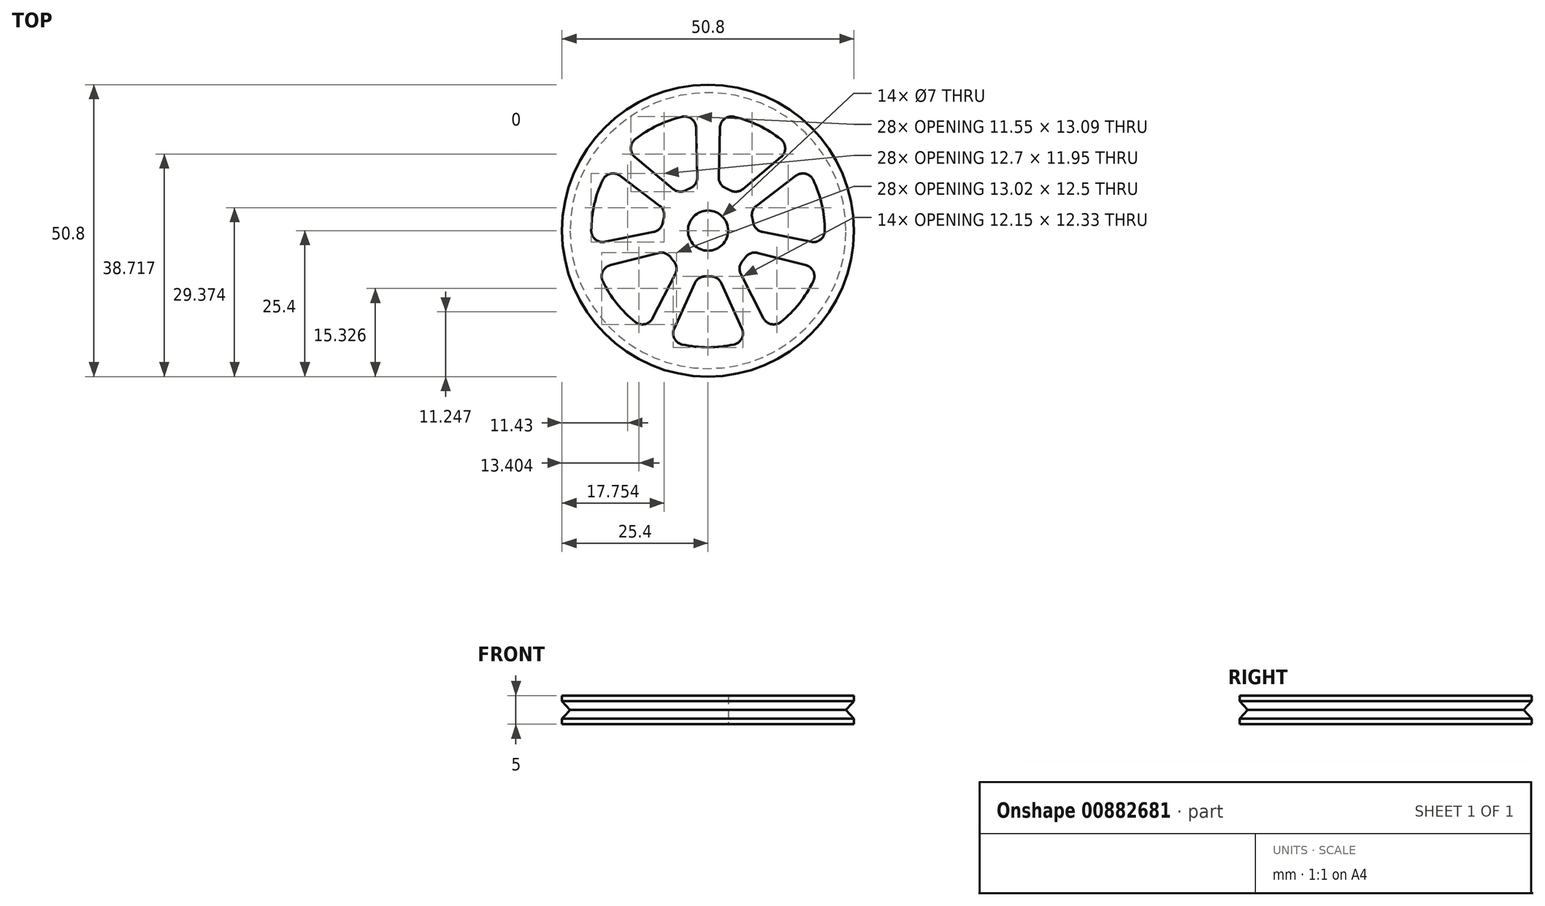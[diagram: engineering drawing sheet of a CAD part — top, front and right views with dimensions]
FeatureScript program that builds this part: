
annotation { "Feature Type Name" : "Feature", "Feature Type Description" : "" }
export const myFeature = defineFeature(function(context is Context, id is Id, definition is map)
    precondition{}
    {
        {
            var Q0;
            Q0=qCreatedBy(makeId("Top.planeOp"),FACE);
            var sketch = newSketch(context, id + "F0", { "sketchPlane" : qUnion([Q0])});
            skCircle(sketch, "E0", {"center": v(0, 0) * mm, "radius": 25.4 * mm});
            skCircle(sketch, "E1", {"center": v(0, 0) * mm, "radius": 3.5 * mm});
            skArc(sketch, "E2.0", {"start": v(-3.1, 7.37) * mm, "mid": v(-3.47, 7.2) * mm, "end": v(-3.83, 7.02) * mm});
            skArc(sketch, "E3.0", {"start": v(-4.52, 19.81) * mm, "mid": v(-8.82, 18.3) * mm, "end": v(-12.67, 15.89) * mm});
            skLineSegment(sketch, "E4.0", {"start": v(-1.87, 9.27) * mm, "end": v(-2.08, 17.9) * mm});
            skLineSegment(sketch, "E5.0", {"start": v(1.87, 9.27) * mm, "end": v(2.08, 17.9) * mm});
            skPoint(sketch, "E6.start.orphan", {"position": v(0, 12.84) * mm});
            skPoint(sketch, "E7.visualSharp", {"position": v(-2.13, 20.2) * mm});
            skArc(sketch, "E7.filletArc", {"start": v(-2.08, 17.9) * mm, "mid": v(-2.85, 19.44) * mm, "end": v(-4.52, 19.81) * mm});
            skPoint(sketch, "E8.visualSharp", {"position": v(-1.83, 7.78) * mm});
            skArc(sketch, "E8.filletArc", {"start": v(-3.1, 7.37) * mm, "mid": v(-2.2, 8.13) * mm, "end": v(-1.87, 9.27) * mm});
            skPoint(sketch, "E9.visualSharp", {"position": v(2.13, 20.2) * mm});
            skArc(sketch, "E9.filletArc", {"start": v(4.52, 19.81) * mm, "mid": v(2.85, 19.44) * mm, "end": v(2.08, 17.9) * mm});
            skPoint(sketch, "E10.visualSharp", {"position": v(1.83, 7.78) * mm});
            skArc(sketch, "E10.filletArc", {"start": v(1.87, 9.27) * mm, "mid": v(2.2, 8.13) * mm, "end": v(3.1, 7.37) * mm});
            skArc(sketch, "E11.1.0", {"start": v(-15.3, 9.54) * mm, "mid": v(-16.97, 9.9) * mm, "end": v(-18.3, 8.82) * mm});
            skLineSegment(sketch, "E11.1.1", {"start": v(-8.4, 4.32) * mm, "end": v(-15.3, 9.54) * mm});
            skArc(sketch, "E11.1.2", {"start": v(-7.7, 2.18) * mm, "mid": v(-7.72, 3.36) * mm, "end": v(-8.4, 4.32) * mm});
            skArc(sketch, "E11.1.3", {"start": v(-6.08, 7.24) * mm, "mid": v(-5, 6.78) * mm, "end": v(-3.83, 7.02) * mm});
            skLineSegment(sketch, "E11.1.4", {"start": v(-6.08, 7.24) * mm, "end": v(-12.7, 12.8) * mm});
            skArc(sketch, "E11.1.5", {"start": v(-12.67, 15.89) * mm, "mid": v(-13.42, 14.35) * mm, "end": v(-12.7, 12.8) * mm});
            skArc(sketch, "E11.2.0", {"start": v(-17, -6.01) * mm, "mid": v(-18.32, -7.1) * mm, "end": v(-18.3, -8.82) * mm});
            skLineSegment(sketch, "E11.2.1", {"start": v(-8.62, -3.88) * mm, "end": v(-17, -6.01) * mm});
            skArc(sketch, "E11.2.2", {"start": v(-6.5, -4.66) * mm, "mid": v(-7.44, -3.94) * mm, "end": v(-8.62, -3.88) * mm});
            skArc(sketch, "E11.2.3", {"start": v(-9.45, -0.24) * mm, "mid": v(-8.41, 0.33) * mm, "end": v(-7.88, 1.38) * mm});
            skLineSegment(sketch, "E11.2.4", {"start": v(-9.45, -0.24) * mm, "end": v(-17.92, -1.96) * mm});
            skArc(sketch, "E11.2.5", {"start": v(-20.32, 0) * mm, "mid": v(-19.59, -1.55) * mm, "end": v(-17.92, -1.96) * mm});
            skArc(sketch, "E11.3.0", {"start": v(-5.9, -17.04) * mm, "mid": v(-5.87, -18.75) * mm, "end": v(-4.52, -19.81) * mm});
            skLineSegment(sketch, "E11.3.1", {"start": v(-2.34, -9.16) * mm, "end": v(-5.9, -17.04) * mm});
            skArc(sketch, "E11.3.2", {"start": v(-0.41, -7.99) * mm, "mid": v(-1.55, -8.28) * mm, "end": v(-2.34, -9.16) * mm});
            skArc(sketch, "E11.3.3", {"start": v(-5.7, -7.54) * mm, "mid": v(-5.5, -6.37) * mm, "end": v(-5.99, -5.3) * mm});
            skLineSegment(sketch, "E11.3.4", {"start": v(-5.7, -7.54) * mm, "end": v(-9.64, -15.23) * mm});
            skArc(sketch, "E11.3.5", {"start": v(-12.67, -15.89) * mm, "mid": v(-11, -16.28) * mm, "end": v(-9.64, -15.23) * mm});
            skArc(sketch, "E11.4.0", {"start": v(9.64, -15.23) * mm, "mid": v(11, -16.28) * mm, "end": v(12.67, -15.89) * mm});
            skLineSegment(sketch, "E11.4.1", {"start": v(5.7, -7.54) * mm, "end": v(9.64, -15.23) * mm});
            skArc(sketch, "E11.4.2", {"start": v(5.99, -5.3) * mm, "mid": v(5.5, -6.37) * mm, "end": v(5.7, -7.54) * mm});
            skArc(sketch, "E11.4.3", {"start": v(2.34, -9.16) * mm, "mid": v(1.55, -8.28) * mm, "end": v(0.41, -7.99) * mm});
            skLineSegment(sketch, "E11.4.4", {"start": v(2.34, -9.16) * mm, "end": v(5.9, -17.04) * mm});
            skArc(sketch, "E11.4.5", {"start": v(4.52, -19.81) * mm, "mid": v(5.87, -18.75) * mm, "end": v(5.9, -17.04) * mm});
            skArc(sketch, "E11.5.0", {"start": v(17.92, -1.96) * mm, "mid": v(19.59, -1.55) * mm, "end": v(20.32, 0) * mm});
            skLineSegment(sketch, "E11.5.1", {"start": v(9.45, -0.24) * mm, "end": v(17.92, -1.96) * mm});
            skArc(sketch, "E11.5.2", {"start": v(7.88, 1.38) * mm, "mid": v(8.41, 0.33) * mm, "end": v(9.45, -0.24) * mm});
            skArc(sketch, "E11.5.3", {"start": v(8.62, -3.88) * mm, "mid": v(7.44, -3.94) * mm, "end": v(6.5, -4.66) * mm});
            skLineSegment(sketch, "E11.5.4", {"start": v(8.62, -3.88) * mm, "end": v(17, -6.01) * mm});
            skArc(sketch, "E11.5.5", {"start": v(18.3, -8.82) * mm, "mid": v(18.32, -7.1) * mm, "end": v(17, -6.01) * mm});
            skArc(sketch, "E11.6.0", {"start": v(12.7, 12.8) * mm, "mid": v(13.42, 14.35) * mm, "end": v(12.67, 15.89) * mm});
            skLineSegment(sketch, "E11.6.1", {"start": v(6.08, 7.24) * mm, "end": v(12.7, 12.8) * mm});
            skArc(sketch, "E11.6.2", {"start": v(3.83, 7.02) * mm, "mid": v(5, 6.78) * mm, "end": v(6.08, 7.24) * mm});
            skArc(sketch, "E11.6.3", {"start": v(8.4, 4.32) * mm, "mid": v(7.72, 3.36) * mm, "end": v(7.7, 2.18) * mm});
            skLineSegment(sketch, "E11.6.4", {"start": v(8.4, 4.32) * mm, "end": v(15.3, 9.54) * mm});
            skArc(sketch, "E11.6.5", {"start": v(18.3, 8.82) * mm, "mid": v(16.97, 9.9) * mm, "end": v(15.3, 9.54) * mm});
            skArc(sketch, "E12.trimOffspring", {"start": v(-7.7, 2.18) * mm, "mid": v(-7.8, 1.78) * mm, "end": v(-7.88, 1.38) * mm});
            skArc(sketch, "E13.trimOffspring", {"start": v(-18.3, 8.82) * mm, "mid": v(-19.81, 4.52) * mm, "end": v(-20.32, 0) * mm});
            skArc(sketch, "E14.trimOffspring", {"start": v(-6.5, -4.66) * mm, "mid": v(-6.25, -4.99) * mm, "end": v(-5.99, -5.3) * mm});
            skArc(sketch, "E15.trimOffspring", {"start": v(-18.3, -8.82) * mm, "mid": v(-15.89, -12.67) * mm, "end": v(-12.67, -15.89) * mm});
            skArc(sketch, "E16.trimOffspring", {"start": v(-4.52, -19.81) * mm, "mid": v(0, -20.32) * mm, "end": v(4.52, -19.81) * mm});
            skArc(sketch, "E17.trimOffspring", {"start": v(-0.41, -7.99) * mm, "mid": v(0, -8) * mm, "end": v(0.41, -7.99) * mm});
            skArc(sketch, "E18.trimOffspring", {"start": v(5.99, -5.3) * mm, "mid": v(6.25, -4.99) * mm, "end": v(6.5, -4.66) * mm});
            skArc(sketch, "E19.trimOffspring", {"start": v(12.67, -15.89) * mm, "mid": v(15.89, -12.67) * mm, "end": v(18.3, -8.82) * mm});
            skArc(sketch, "E20.trimOffspring", {"start": v(20.32, 0) * mm, "mid": v(19.81, 4.52) * mm, "end": v(18.3, 8.82) * mm});
            skArc(sketch, "E21.trimOffspring", {"start": v(7.88, 1.38) * mm, "mid": v(7.8, 1.78) * mm, "end": v(7.7, 2.18) * mm});
            skArc(sketch, "E22.trimOffspring", {"start": v(3.83, 7.02) * mm, "mid": v(3.47, 7.2) * mm, "end": v(3.1, 7.37) * mm});
            skArc(sketch, "E23.trimOffspring", {"start": v(12.67, 15.89) * mm, "mid": v(8.82, 18.3) * mm, "end": v(4.52, 19.81) * mm});
            skSolve(sketch);
        }
        {
            var Q0;
            Q0=makeQuery(id+"F0.imprint","IMPRINT",FACE,{"disambiguationData":[TD([[makeQuery(id+"F0.imprint","IMPRINT",EDGE,{"derivedFrom":sQuery(id+"F0.wireOp",EDGE,"E0")}),1.0]])]});
            extrude(context, id + "F1", {"entities" : qUnion([Q0]), "endBound" : BoundingType.SYMMETRIC, "depth" : 5 * mm, "offsetDistance" : 25.4 * mm});
        }
        {
            var Q0;
            Q0=qCreatedBy(makeId("Right.planeOp"),FACE);
            var sketch = newSketch(context, id + "F2", { "sketchPlane" : qUnion([Q0])});
            skLineSegment(sketch, "E24", {"start": v(25.5, 0) * mm, "end": v(24, 0) * mm});
            skLineSegment(sketch, "E25", {"start": v(24, 0) * mm, "end": v(25.4, -1.55) * mm});
            skLineSegment(sketch, "E26", {"start": v(25.4, -1.55) * mm, "end": v(25.5, 0) * mm});
            skLineSegment(sketch, "E27.MirrorCS", {"start": v(24, 0) * mm, "end": v(25.4, 1.55) * mm});
            skLineSegment(sketch, "E28.MirrorCS", {"start": v(25.4, 1.55) * mm, "end": v(25.5, 0) * mm});
            skLineSegment(sketch, "E29", {"start": v(0, -12.13) * mm, "end": v(0, 15.65) * mm, "construction": true});
            skSolve(sketch);
        }
        {
            var Q0;
            Q0 = qSketchRegion(id + "F2", true);
            var Q1;
            Q1=sQuery(id+"F2.wireOp",EDGE,"E29");
            revolve(context, id + "F3", {"operationType" : NewBodyOperationType.REMOVE, "surfaceOperationType" : NewSurfaceOperationType.NEW, "entities" : qUnion([Q0]), "axis" : qUnion([Q1]), "revolveType" : RevolveType.FULL, "oppositeDirection" : true});
        }
    });
